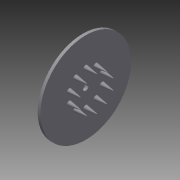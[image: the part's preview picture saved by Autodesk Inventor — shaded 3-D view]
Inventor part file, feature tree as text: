
AUTODESK INVENTOR PART (.ipt)
format: ipt  version: 2015 (Build 190159000, 159)  size: 174,592 bytes
history: native  units: in
note: dims shown in document units (in); Inventor stores cm internally (conversion verified against a paired STEP export)
features: extrude x7, sketch x7, pattern_circular x3, reference x1
ambient origin geometry x8: Origin, YZ Plane, XZ Plane, XY Plane, X Axis, Y Axis, Z Axis, Center Point
bodies: Solid1 (feature_tree)
feature tree (18):
  extrude  "Extrusion1"  Depth=0.125in TaperAngle=0.0deg
  extrude  "Extrusion2"  Depth=0.5in
  pattern_circular  "Circular Pattern1"  Count=10 Angle=360.0deg
  extrude  "Extrusion3"  Depth=0.5in TaperAngle=360.0deg
  pattern_circular  "Circular Pattern2"  [2 undecoded]
  extrude  "Extrusion4"  Depth=0.4375in
  extrude  "Extrusion5"  Depth=0.4375in TaperAngle=360.0deg
  extrude  "Extrusion6"  [1 undecoded]
  extrude  "Extrusion7"  [1 undecoded]
  pattern_circular  "Circular Pattern3"  [2 undecoded]
  sketch  "Sketch1"  dims[d0=4.0in d1=0.125in d2=0.0in]
  sketch  "Sketch2"  dims[d3=0.2in d4=0.5in d5=-0.0687in d6=3.937in d7=360.0deg]
  sketch  "Sketch3"  dims[d9=0.5in d10=-0.0687in d11=2.3622in d12=360.0deg]
  sketch  "Sketch4"  dims[d14=0.43in]
  sketch  "Sketch5"  dims[d15=0.125in d16=0.0in]
  sketch  "Sketch6"  dims[d17=0.25in]
  reference  "Reference1"
  sketch  "Sketch7"  dims[d18=0.125in d19=0.0in d20=1.0in d21=0.0in d22=0.4375in d23=-0.0825in d24=4.7244in d25=360.0deg]
note: 6 required parameter values undecoded (feature->parameter linkage not recoverable at this tier; creation-order binding heuristic only, values carry confidence <= 0.55)
